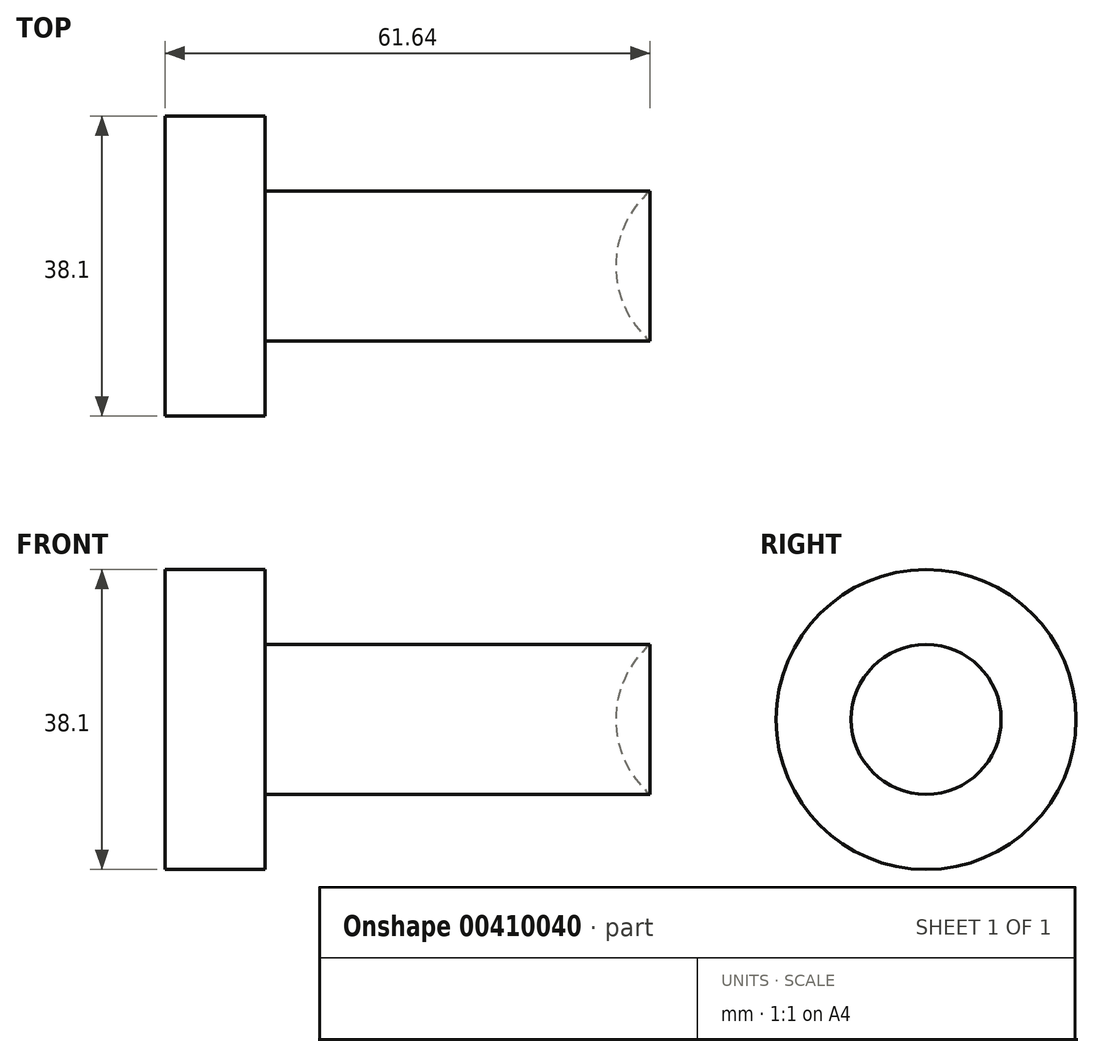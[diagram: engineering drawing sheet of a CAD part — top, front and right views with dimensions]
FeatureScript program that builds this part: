
annotation { "Feature Type Name" : "Feature", "Feature Type Description" : "" }
export const myFeature = defineFeature(function(context is Context, id is Id, definition is map)
    precondition{}
    {
        {
            var Q0;
            Q0=qCreatedBy(makeId("Front.planeOp"),FACE);
            var sketch = newSketch(context, id + "F0", { "sketchPlane" : qUnion([Q0])});
            skLineSegment(sketch, "E0", {"start": v(-51.86, 0) * mm, "end": v(66.15, 0) * mm, "construction": true});
            skLineSegment(sketch, "E1.bottom", {"start": v(-12.7, 0) * mm, "end": v(0, 0) * mm});
            skLineSegment(sketch, "E1.top", {"start": v(-12.7, 19.05) * mm, "end": v(0, 19.05) * mm});
            skLineSegment(sketch, "E1.left", {"start": v(-12.7, 0) * mm, "end": v(-12.7, 19.05) * mm});
            skLineSegment(sketch, "E1.right", {"start": v(0, 0) * mm, "end": v(0, 19.05) * mm});
            skLineSegment(sketch, "E2.bottom", {"start": v(0, 9.52) * mm, "end": v(50.8, 9.52) * mm});
            skLineSegment(sketch, "E2.top", {"start": v(0, 0) * mm, "end": v(50.8, 0) * mm});
            skLineSegment(sketch, "E2.left", {"start": v(0, 9.53) * mm, "end": v(0, 0) * mm});
            skLineSegment(sketch, "E2.right", {"start": v(50.8, 9.52) * mm, "end": v(50.8, 0) * mm});
            skSolve(sketch);
        }
        {
            var Q0;
            Q0 = qSketchRegion(id + "F0", true);
            var Q1;
            Q1=sQuery(id+"F0.wireOp",EDGE,"E0");
            revolve(context, id + "F1", {"entities" : qUnion([Q0]), "axis" : qUnion([Q1]), "revolveType" : RevolveType.FULL});
        }
        {
            var Q0;
            Q0=qCreatedBy(makeId("Front.planeOp"),FACE);
            var sketch = newSketch(context, id + "F2", { "sketchPlane" : qUnion([Q0])});
            skLineSegment(sketch, "E3", {"start": v(57.15, 21.6) * mm, "end": v(57.15, -17.17) * mm, "construction": true});
            skArc(sketch, "E4", {"start": v(57.15, -12.57) * mm, "mid": v(69.72, 0) * mm, "end": v(57.15, 12.57) * mm});
            skLineSegment(sketch, "E5", {"start": v(57.15, 12.57) * mm, "end": v(57.15, -12.57) * mm});
            skSolve(sketch);
        }
        {
            var Q0;
            Q0 = qSketchRegion(id + "F2", true);
            var Q1;
            Q1=sQuery(id+"F2.wireOp",EDGE,"E3");
            revolve(context, id + "F3", {"operationType" : NewBodyOperationType.REMOVE, "entities" : qUnion([Q0]), "axis" : qUnion([Q1]), "revolveType" : RevolveType.FULL});
        }
    });
